# Revit family: Zumtobel PANOS INF - Q100L
name_source: partatom
category: Leuchten
revit_build: Autodesk Revit 2016 (Build: 20150220_1215(x64)
units: mm (PartAtom-declared; Revit-internal decimal feet)

## family parameters
Basisbauteil = Fläche
Beim Laden mit Abzugskörper schneiden = Nein
Bemaßung runder Anschluss = Durchmesser verwenden
Gemeinsam genutzt = Nein
Lichtquelle = Ja
OmniClass-Nummer = 23.80.70.11
OmniClass-Titel = Luminaries for Internal Lighting
Raumberechnungspunkt = Nein
Teiletyp = Normal

## types (2) — shared parameters
Baugruppenkennzeichen = D5020200
Beschreibung = Ceiling-recessed LED downlight with smooth optic
Construction Height = 53 mm  [stored 0.173885 ft]
Cover = Nein
Datei für fotometrisches Netz = 60817883_(STD_LEO).IES
Emissionsform beim Rendern sichtbar = Ja
Farbfilter = 16777215
Farbtemperaturverschiebung bei Dämpfen der Lampe = <Keine Auswahl>
Height = 100 mm  [stored 0.328084 ft]
Hersteller = Zumtobel Lighting
Lampe = LED
Length = 100 mm  [stored 0.328084 ft]
Neigungswinkel = -90.00°
Opening Height = 117 mm  [stored 0.383858 ft]
URL = http://www.zumtobel.com
Voltage = 230 V
Von Breite des Rechtecks ausssenden = 91 mm  [stored 0.298556 ft]
Von Länge des Rechtecks aussenden = 91 mm  [stored 0.298556 ft]
Width = 100 mm  [stored 0.328084 ft]
zero-valued in all types: Vorgabe-Ansicht

## per-type parameters (varying)
| type | Modell | Scheinlast |
| P-INF Q100L 1000 | 60817883 | 9 VA |
| P-INF Q100L 1600 | 60817943 | 15 VA |

note: [stored X ft] marks values corroborated as IEEE doubles in the binary element streams (Revit-internal decimal feet)

## geometry (parser evidence)
native form markers: Sweep x3
no freeform markers — native parametric forms only
